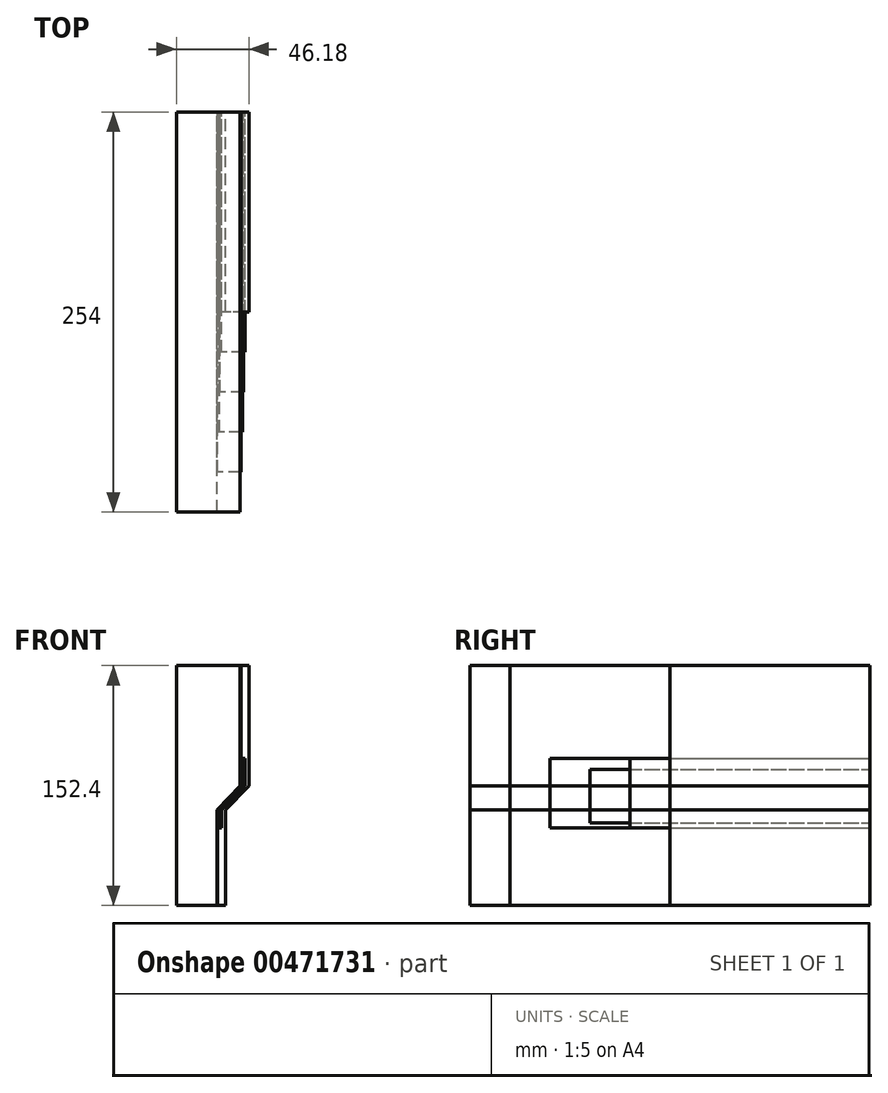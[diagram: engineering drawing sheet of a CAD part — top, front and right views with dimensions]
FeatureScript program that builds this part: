
annotation { "Feature Type Name" : "Feature", "Feature Type Description" : "" }
export const myFeature = defineFeature(function(context is Context, id is Id, definition is map)
    precondition{}
    {
        {
            var Q0;
            Q0=qCreatedBy(makeId("Front.planeOp"),FACE);
            var sketch = newSketch(context, id + "F0", { "sketchPlane" : qUnion([Q0])});
            skLineSegment(sketch, "E0.bottom", {"start": v(-76.22, 76.43) * mm, "end": v(-50.4, 76.43) * mm});
            skLineSegment(sketch, "E0.top", {"start": v(-76.22, -75.97) * mm, "end": v(-50.4, -75.97) * mm});
            skLineSegment(sketch, "E0.left", {"start": v(-76.22, 76.43) * mm, "end": v(-76.22, -75.97) * mm});
            skLineSegment(sketch, "E0.right", {"start": v(-50.4, 76.43) * mm, "end": v(-50.4, -75.97) * mm});
            skLineSegment(sketch, "E1.bottom", {"start": v(-50.4, 76.43) * mm, "end": v(-35.63, 76.43) * mm});
            skLineSegment(sketch, "E1.top", {"start": v(-50.4, 0) * mm, "end": v(-35.63, 0) * mm});
            skLineSegment(sketch, "E1.left", {"start": v(-50.4, 76.43) * mm, "end": v(-50.4, 0) * mm});
            skLineSegment(sketch, "E1.right", {"start": v(-35.63, 76.43) * mm, "end": v(-35.63, 0) * mm});
            skLineSegment(sketch, "E2", {"start": v(-35.63, 0) * mm, "end": v(-50.4, -15.32) * mm});
            skLineSegment(sketch, "E3", {"start": v(-35.63, 76.43) * mm, "end": v(-35.12, 76.43) * mm});
            skLineSegment(sketch, "E4", {"start": v(-35.12, 76.43) * mm, "end": v(-35.12, 0) * mm});
            skLineSegment(sketch, "E5", {"start": v(-35.12, 0) * mm, "end": v(-49.9, -15.32) * mm});
            skLineSegment(sketch, "E6", {"start": v(-49.9, -15.32) * mm, "end": v(-49.9, -75.97) * mm});
            skLineSegment(sketch, "E7", {"start": v(-49.9, -75.97) * mm, "end": v(-50.4, -75.97) * mm});
            skLineSegment(sketch, "E8", {"start": v(-35.12, 17.5) * mm, "end": v(-34.1, 17.5) * mm});
            skLineSegment(sketch, "E9", {"start": v(-34.1, 17.5) * mm, "end": v(-34.1, 0) * mm});
            skLineSegment(sketch, "E10", {"start": v(-34.1, 0) * mm, "end": v(-48.88, -15.32) * mm});
            skLineSegment(sketch, "E11", {"start": v(-48.88, -15.32) * mm, "end": v(-48.88, -26.67) * mm});
            skLineSegment(sketch, "E12", {"start": v(-48.88, -26.67) * mm, "end": v(-49.9, -26.67) * mm});
            skLineSegment(sketch, "E13", {"start": v(-34.1, 10.34) * mm, "end": v(-33.6, 10.34) * mm});
            skLineSegment(sketch, "E14", {"start": v(-33.6, 10.34) * mm, "end": v(-33.6, 0) * mm});
            skLineSegment(sketch, "E15", {"start": v(-33.6, 0) * mm, "end": v(-48.37, -15.32) * mm});
            skLineSegment(sketch, "E16", {"start": v(-48.37, -15.32) * mm, "end": v(-48.37, -23.4) * mm});
            skLineSegment(sketch, "E17", {"start": v(-48.37, -23.4) * mm, "end": v(-48.88, -23.4) * mm});
            skLineSegment(sketch, "E18", {"start": v(-34.1, 17.5) * mm, "end": v(-32.58, 17.5) * mm});
            skLineSegment(sketch, "E19", {"start": v(-32.58, 17.5) * mm, "end": v(-32.58, 0) * mm});
            skLineSegment(sketch, "E20", {"start": v(-32.58, 0) * mm, "end": v(-47.36, -15.32) * mm});
            skLineSegment(sketch, "E21", {"start": v(-47.36, -15.32) * mm, "end": v(-47.36, -26.67) * mm});
            skLineSegment(sketch, "E22", {"start": v(-47.36, -26.67) * mm, "end": v(-48.88, -26.67) * mm});
            skLineSegment(sketch, "E23", {"start": v(-35.12, 76.43) * mm, "end": v(-30.04, 76.43) * mm});
            skLineSegment(sketch, "E24", {"start": v(-30.04, 76.43) * mm, "end": v(-30.04, 0) * mm});
            skLineSegment(sketch, "E25", {"start": v(-30.04, 0) * mm, "end": v(-44.82, -15.32) * mm});
            skLineSegment(sketch, "E26", {"start": v(-44.82, -15.32) * mm, "end": v(-44.82, -75.97) * mm});
            skLineSegment(sketch, "E27", {"start": v(-44.82, -75.97) * mm, "end": v(-49.9, -75.97) * mm});
            skSolve(sketch);
        }
        {
            var Q0;
            Q0=makeQuery(id+"F0.imprint","IMPRINT",FACE,{"disambiguationData":[TD([[makeQuery(id+"F0.imprint","IMPRINT",EDGE,{"derivedFrom":sQuery(id+"F0.wireOp",EDGE,"E0.bottom")}),-1.0]])]});
            extrude(context, id + "F1", {"entities" : qUnion([Q0]), "depth" : 254 * mm});
        }
        {
            var Q0;
            Q0=makeQuery(id+"F0.imprint","IMPRINT",FACE,{"disambiguationData":[TD([[makeQuery(id+"F0.imprint","IMPRINT",EDGE,{"derivedFrom":sQuery(id+"F0.wireOp",EDGE,"E1.bottom")}),-1.0]])]});
            extrude(context, id + "F2", {"entities" : qUnion([Q0]), "depth" : 254 * mm});
        }
        {
            var Q0;
            {var subQ0=sQuery(id+"F0.wireOp",EDGE,"E1.top");Q0=makeQuery(id+"F0.imprint","IMPRINT",FACE,{"disambiguationData":[TD([[makeQuery(id+"F0.imprint","IMPRINT",EDGE,{"derivedFrom":subQ0}),-1.0]])]});}
            extrude(context, id + "F3", {"entities" : qUnion([Q0]), "operationType" : NewBodyOperationType.ADD, "depth" : 254 * mm});
        }
        {
            var Q0;
            Q0=makeQuery(id+"F0.imprint","IMPRINT",FACE,{"disambiguationData":[TD([[makeQuery(id+"F0.imprint","IMPRINT",EDGE,{"derivedFrom":sQuery(id+"F0.wireOp",EDGE,"E1.right")}),1.0]])]});
            extrude(context, id + "F4", {"entities" : qUnion([Q0]), "depth" : 228.6 * mm});
        }
        {
            var Q0;
            {var subQ1=sQuery(id+"F0.wireOp",EDGE,"E5");Q0=makeQuery(id+"F0.imprint","IMPRINT",FACE,{"disambiguationData":[TD([[makeQuery(id+"F0.imprint","IMPRINT",EDGE,{"derivedFrom":subQ1}),1.0]])]});}
            extrude(context, id + "F5", {"entities" : qUnion([Q0]), "depth" : 203.2 * mm});
        }
        {
            var Q0;
            {var subQ1=sQuery(id+"F0.wireOp",EDGE,"E10");Q0=makeQuery(id+"F0.imprint","IMPRINT",FACE,{"disambiguationData":[TD([[makeQuery(id+"F0.imprint","IMPRINT",EDGE,{"derivedFrom":subQ1}),1.0]])]});}
            extrude(context, id + "F6", {"entities" : qUnion([Q0]), "depth" : 177.8 * mm});
        }
        {
            var Q0;
            {var subQ3=sQuery(id+"F0.wireOp",EDGE,"E13");Q0=makeQuery(id+"F0.imprint","IMPRINT",FACE,{"disambiguationData":[TD([[makeQuery(id+"F0.imprint","IMPRINT",EDGE,{"derivedFrom":subQ3}),1.0]])]});}
            extrude(context, id + "F7", {"entities" : qUnion([Q0]), "depth" : 152.4 * mm});
        }
        {
            var Q0;
            {var subQ2=sQuery(id+"F0.wireOp",EDGE,"E8");Q0=makeQuery(id+"F0.imprint","IMPRINT",FACE,{"disambiguationData":[TD([[makeQuery(id+"F0.imprint","IMPRINT",EDGE,{"derivedFrom":subQ2}),1.0]])]});}
            extrude(context, id + "F8", {"entities" : qUnion([Q0]), "depth" : 127 * mm});
        }
    });
